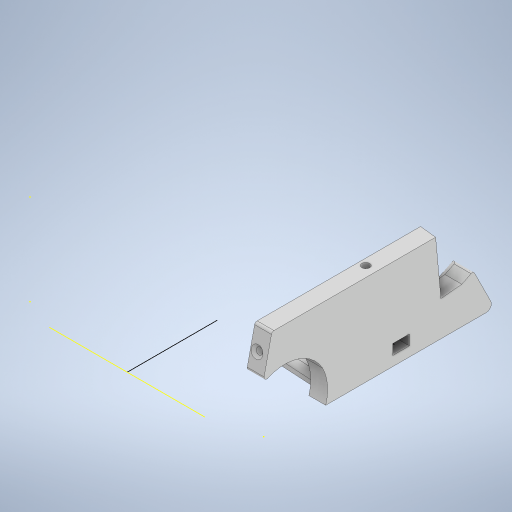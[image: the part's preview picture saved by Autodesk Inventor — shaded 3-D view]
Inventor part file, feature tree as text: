
AUTODESK INVENTOR PART (.ipt)
format: ipt  version: 2023 (Build 270158000, 158)  size: 2,900,992 bytes
history: native  units: mm
features: projected_geometry x144, extrude x133, sketch x99, fillet x14, reference x6, other x5, plane x3, mirror x3, chamfer x2
ambient origin geometry x8: Origin, YZ Plane, XZ Plane, XY Plane, X Axis, Y Axis, Z Axis, Center Point
bodies: Solid1 (feature_tree)
feature tree (409):
  sketch  "Sketch1"  dims[d0=100.0mm d1=100.0mm]
  extrude  "Extrusion1"  Depth=100.0mm
  extrude  "Extrusion2"  Depth=20.0mm
  extrude  "Extrusion3"  Depth=20.0mm
  sketch  "Sketch3"  dims[d4=31.0mm d5=20.0mm]
  extrude  "Extrusion4"  Depth=19.0mm
  extrude  "Extrusion5"  Depth=10.0mm
  sketch  "Sketch4"  dims[d6=14.0mm d7=19.0mm]
  plane  "Work Plane1"
  mirror  "Mirror1"
  extrude  "Extrusion6"  Depth=10.0mm
  sketch  "Sketch8"  dims[d10=10.0mm d11=2.0mm]
  extrude  "Extrusion7"  Depth=15.0mm
  extrude  "Extrusion8"  Depth=2.0mm
  extrude  "Extrusion9"  Depth=5.0mm
  sketch  "Sketch9"  dims[d12=2.0mm d13=15.0mm]
  extrude  "Extrusion10"  Depth=10.0mm TaperAngle=0.0deg
  extrude  "Extrusion11"  TaperAngle=0.0deg  [1 undecoded]
  sketch  "Sketch10"  dims[d14=15.0mm d15=2.0mm]
  extrude  "Extrusion12"  Depth=14.0mm TaperAngle=0.0deg
  extrude  "Extrusion13"  TaperAngle=90.0deg  [1 undecoded]
  extrude  "Extrusion14"  Depth=40.0mm
  sketch  "Sketch12"  dims[d18=10.0mm d19=0.0mm d20=2.0mm d21=0.0mm]
  extrude  "Extrusion15"  Depth=25.0mm
  extrude  "Extrusion16"  Depth=5.0mm
  extrude  "Extrusion17"  Depth=13.0mm
  extrude  "Extrusion18"  Depth=8.0mm
  extrude  "Extrusion19"  Depth=18.0mm TaperAngle=0.0deg
  extrude  "Extrusion20"  Depth=49.0mm
  extrude  "Extrusion21"  Depth=5.0mm
  sketch  "Sketch15"  dims[d28=14.25mm d29=0.0mm d30=90.0deg]
  plane  "Work Plane2"
  mirror  "Mirror2"
  extrude  "Extrusion22"  TaperAngle=0.0deg  [1 undecoded]
  sketch  "Sketch17"  dims[d36=15.0mm d37=25.0mm]
  extrude  "Extrusion23"  Depth=10.0mm
  extrude  "Extrusion24"  Depth=1.6mm
  extrude  "Extrusion25"  TaperAngle=0.0deg  [1 undecoded]
  extrude  "Extrusion26"  Depth=14.0mm TaperAngle=0.0deg
  extrude  "Extrusion27"  Depth=6.0mm
  sketch  "Sketch21"  dims[d44=18.0mm d45=0.0mm d46=18.0mm d47=0.0mm]
  extrude  "Extrusion28"  Depth=2.0mm
  extrude  "Extrusion29"  Depth=6.0mm TaperAngle=0.0deg
  sketch  "Sketch22"  dims[d48=0.0mm d49=0.0mm d50=49.0mm]
  extrude  "Extrusion30"  Depth=15.0mm TaperAngle=0.0deg
  extrude  "Extrusion31"  Depth=3.2mm
  extrude  "Extrusion32"  Depth=4.0mm
  extrude  "Extrusion33"  Depth=1.0mm TaperAngle=0.0deg
  extrude  "Extrusion34"  Depth=3.0mm
  extrude  "Extrusion35"  Depth=15.0mm TaperAngle=0.0deg
  extrude  "Extrusion36"  Depth=3.2mm
  fillet  "Face Fillet1"
  fillet  "Face Fillet2"
  extrude  "Extrusion37"  Depth=3.2mm
  fillet  "Face Fillet3"
  fillet  "Face Fillet5"
  extrude  "Extrusion38"  Depth=5.0mm TaperAngle=0.0deg
  extrude  "Extrusion39"  TaperAngle=0.0deg  [1 undecoded]
  fillet  "Fillet2"  Radius=2.8mm
  extrude  "Extrusion40"  Depth=100.0mm TaperAngle=0.0deg
  sketch  "Sketch32"  dims[d76=6.0mm d77=0.0mm d78=15.0mm d79=0.0mm]
  extrude  "Extrusion41"  Depth=11.0mm
  extrude  "Extrusion42"  Depth=9.0mm TaperAngle=0.0deg
  extrude  "Extrusion43"  Depth=3.2mm
  sketch  "Sketch33"  dims[d80=15.0mm d81=0.0mm d82=3.2mm]
  extrude  "Extrusion44"  Depth=7.0mm TaperAngle=0.0deg
  extrude  "Extrusion45"  Depth=40.656mm TaperAngle=0.0deg
  extrude  "Extrusion46"  Depth=9.0mm TaperAngle=0.0deg
  extrude  "Extrusion47"  Depth=3.0mm
  sketch  "Sketch36"  dims[d91=90.0deg d92=3.0mm]
  extrude  "Extrusion48"  Depth=1.5mm TaperAngle=0.0deg
  extrude  "Extrusion49"  Depth=6.0mm
  sketch  "Sketch37"  dims[d93=3.0mm d94=15.0mm d95=0.0mm]
  extrude  "Extrusion50"  Depth=10.0mm TaperAngle=0.0deg
  extrude  "Extrusion51"  Depth=4.0mm
  extrude  "Extrusion52"  Depth=10.0mm TaperAngle=0.0deg
  extrude  "Extrusion53"  Depth=20.0mm TaperAngle=0.0deg
  sketch  "Sketch40"  dims[d100=4.0mm d101=5.0mm d102=0.0mm]
  extrude  "Extrusion54"  Depth=1.5mm
  extrude  "Extrusion55"  Depth=3.0mm
  extrude  "Extrusion56"  Depth=6.4mm
  extrude  "Extrusion57"  Depth=3.0mm
  fillet  "Fillet3"  Radius=2.0mm
  extrude  "Extrusion58"  TaperAngle=0.0deg  [1 undecoded]
  sketch  "Sketch44"  dims[d114=3.4mm d115=9.0mm d116=0.0mm]
  extrude  "Extrusion59"  TaperAngle=0.0deg  [1 undecoded]
  extrude  "Extrusion60"  Depth=10.0mm TaperAngle=0.0deg
  sketch  "Sketch45"  dims[d117=15.0mm d118=0.0mm d119=3.2mm]
  extrude  "Extrusion61"  Depth=10.0mm TaperAngle=0.0deg
  extrude  "Extrusion62"  Depth=3.0mm
  sketch  "Sketch46"  dims[d120=3.2mm d121=7.0mm d122=0.0mm]
  extrude  "Extrusion63"  Depth=6.5mm TaperAngle=0.0deg
  extrude  "Extrusion64"  Depth=17.0mm TaperAngle=0.0deg
  extrude  "Extrusion65"  Depth=3.0mm
  extrude  "Extrusion66"  Depth=5.0mm TaperAngle=0.0deg
  sketch  "Sketch49"  dims[d138=28.734mm d139=3.0mm]
  extrude  "Extrusion67"  Depth=6.5mm TaperAngle=0.0deg
  extrude  "Extrusion68"  Depth=14.0mm TaperAngle=0.0deg
  extrude  "Extrusion69"  Depth=2.0mm
  extrude  "Extrusion70"  Depth=16.0mm TaperAngle=0.0deg
  extrude  "Extrusion71"  Depth=17.0mm TaperAngle=0.0deg
  extrude  "Extrusion72"  Depth=2.5mm
  extrude  "Extrusion73"  Depth=2.0mm
  extrude  "Extrusion74"  TaperAngle=0.0deg  [1 undecoded]
  extrude  "Extrusion75"  Depth=3.0mm TaperAngle=0.0deg
  extrude  "Extrusion76"  Depth=2.5mm
  sketch  "Sketch53"  dims[d149=6.7mm d152=4.0mm]
  extrude  "Extrusion77"  Depth=1.0mm
  extrude  "Extrusion78"  Depth=3.0mm
  extrude  "Extrusion79"  Depth=15.0mm TaperAngle=0.0deg
  extrude  "Extrusion80"  Depth=10.0mm TaperAngle=0.0deg
  extrude  "Extrusion81"  Depth=10.0mm TaperAngle=0.0deg
  extrude  "Extrusion82"  Depth=4.0mm TaperAngle=0.0deg
  extrude  "Extrusion83"  Depth=10.0mm TaperAngle=0.0deg
  sketch  "Sketch59"  dims[d166=6.4mm d167=3.0mm d169=2.0mm]
  extrude  "Extrusion84"  Depth=7.0mm
  extrude  "Extrusion85"  Depth=3.0mm TaperAngle=0.0deg
  extrude  "Extrusion86"  Depth=4.0mm TaperAngle=0.0deg
  extrude  "Extrusion87"  Depth=1.0mm
  extrude  "Extrusion88"  Depth=10.0mm
  sketch  "Sketch62"  dims[d178=10.0mm d179=0.0mm d180=4.0mm d181=0.0mm]
  extrude  "Extrusion89"  Depth=30.0mm TaperAngle=0.0deg
  extrude  "Extrusion90"  Depth=2.5mm
  fillet  "Fillet4"  Radius=11.0mm
  extrude  "Extrusion91"  TaperAngle=0.0deg  [1 undecoded]
  extrude  "Extrusion92"  Depth=10.0mm
  extrude  "Extrusion93"  Depth=3.0mm
  extrude  "Extrusion94"  Depth=1.0mm TaperAngle=0.0deg
  extrude  "Extrusion95"  Depth=1.5mm TaperAngle=0.0deg
  sketch  "Sketch68"  dims[d205=4.0mm d206=0.0mm d207=5.0mm d208=0.0mm]
  extrude  "Extrusion96"  Depth=10.0mm TaperAngle=0.0deg
  extrude  "Extrusion97"  Depth=10.0mm TaperAngle=0.0deg
  extrude  "Extrusion98"  Depth=10.0mm
  extrude  "Extrusion99"  Depth=10.0mm TaperAngle=0.0deg
  extrude  "Extrusion100"  Depth=10.0mm TaperAngle=0.0deg
  sketch  "Sketch74"  dims[d219=6.5mm d220=0.0mm d221=16.0mm d222=0.0mm]
  extrude  "Extrusion101"  Depth=10.0mm TaperAngle=0.0deg
  extrude  "Extrusion102"  Depth=10.0mm
  extrude  "Extrusion103"  Depth=10.0mm TaperAngle=0.0deg
  extrude  "Extrusion104"  Depth=10.0mm TaperAngle=0.0deg
  extrude  "Extrusion105"  Depth=10.0mm
  fillet  "Fillet6"  Radius=1.5mm
  fillet  "Fillet7"  Radius=3.5mm
  extrude  "Extrusion106"  Depth=10.0mm
  fillet  "Fillet8"  Radius=6.5mm
  extrude  "Extrusion107"  Depth=10.0mm TaperAngle=0.0deg
  sketch  "Sketch80"  dims[d239=1.0mm d240=2.5mm]
  extrude  "Extrusion108"  Depth=10.0mm
  extrude  "Extrusion109"  Depth=10.0mm TaperAngle=0.0deg
  extrude  "Extrusion110"  Depth=10.0mm TaperAngle=0.0deg
  extrude  "Extrusion111"  Depth=10.0mm
  extrude  "Extrusion112"  TaperAngle=90.0deg  [1 undecoded]
  fillet  "Fillet9"  Radius=2.7mm
  extrude  "Extrusion113"  Depth=10.0mm TaperAngle=0.0deg
  extrude  "Extrusion114"  Depth=10.0mm
  extrude  "Extrusion115"  Depth=10.0mm TaperAngle=0.0deg
  plane  "Work Plane3"
  mirror  "Mirror3"
  extrude  "Extrusion116"  Depth=10.0mm TaperAngle=0.0deg
  extrude  "Extrusion117"  Depth=10.0mm TaperAngle=0.0deg
  sketch  "Sketch89"  dims[d269=6.5mm d270=0.0mm d271=3.0mm d272=0.0mm]
  extrude  "Extrusion118"  Depth=10.0mm TaperAngle=0.0deg
  extrude  "Extrusion119"  Depth=10.0mm TaperAngle=0.0deg
  extrude  "Extrusion120"  Depth=10.0mm
  chamfer  "Chamfer1"  Distance=1.0mm
  sketch  "Sketch93"  dims[d282=45.0mm d283=30.0mm d284=0.0mm]
  extrude  "Extrusion121"  Depth=10.0mm TaperAngle=0.0deg
  extrude  "Extrusion122"  Depth=10.0mm
  extrude  "Extrusion123"  Depth=10.0mm
  extrude  "Extrusion124"  Depth=10.0mm TaperAngle=0.0deg
  extrude  "Extrusion125"  Depth=10.0mm TaperAngle=0.0deg
  extrude  "Extrusion126"  Depth=10.0mm TaperAngle=0.0deg
  extrude  "Extrusion127"  Depth=10.0mm TaperAngle=0.0deg
  fillet  "Fillet10"  Radius=6.5mm
  extrude  "Extrusion128"  Depth=10.0mm TaperAngle=0.0deg
  extrude  "Extrusion129"  Depth=10.0mm
  extrude  "Extrusion130"  Depth=10.0mm
  fillet  "Fillet11"  Radius=10.0mm
  fillet  "Fillet12"  Radius=15.0mm
  chamfer  "Chamfer2"  Distance=12.0mm
  extrude  "Wyciągnięcie proste131"  Depth=10.0mm
  extrude  "Wyciągnięcie proste132"  Depth=10.0mm
  extrude  "Wyciągnięcie proste133"  Depth=10.0mm
  sketch  "Sketch2"  dims[d2=5.0mm d3=20.0mm]
  projected_geometry  "Projected Loop1"
  sketch  "Sketch6"  dims[d8=10.0mm d9=14.0mm]
  projected_geometry  "Projected Loop5"
  projected_geometry  "Projected Loop6"
  projected_geometry  "Projected Loop7"
  projected_geometry  "Projected Loop8"
  projected_geometry  "Projected Loop9"
  projected_geometry  "Projected Loop10"
  sketch  "Sketch11"  dims[d16=1.0mm d17=5.0mm]
  projected_geometry  "Projected Loop11"
  projected_geometry  "Projected Loop12"
  sketch  "Sketch13"  dims[d22=31.0mm d23=0.0mm d24=0.0mm]
  projected_geometry  "Projected Loop13"
  projected_geometry  "Projected Loop14"
  sketch  "Sketch14"  dims[d25=30.4mm d26=14.0mm d27=0.0mm]
  projected_geometry  "Projected Loop15"
  projected_geometry  "Projected Loop16"
  sketch  "Sketch16"  dims[d33=25.0mm d34=0.0mm d35=40.0mm]
  projected_geometry  "Projected Loop17"
  projected_geometry  "Projected Loop18"
  projected_geometry  "Projected Loop19"
  sketch  "Sketch18"  dims[d38=20.0mm d39=5.0mm]
  projected_geometry  "Projected Loop20"
  projected_geometry  "Projected Loop21"
  projected_geometry  "Projected Loop22"
  projected_geometry  "Projected Loop23"
  projected_geometry  "Projected Loop24"
  projected_geometry  "Projected Loop25"
  projected_geometry  "Projected Loop26"
  sketch  "Sketch19"  dims[d40=7.0mm d41=13.0mm]
  projected_geometry  "Projected Loop27"
  sketch  "Sketch20"  dims[d42=7.0mm d43=8.0mm]
  projected_geometry  "Projected Loop28"
  projected_geometry  "Projected Loop29"
  projected_geometry  "Projected Loop30"
  sketch  "Sketch23"  dims[d51=25.0mm d52=5.0mm]
  sketch  "Sketch24"  dims[d53=20.0mm d54=0.0mm d55=0.0mm]
  projected_geometry  "Projected Loop31"
  projected_geometry  "Projected Loop32"
  sketch  "Sketch25"  dims[d56=10.0mm d57=0.0mm d58=1.6mm]
  projected_geometry  "Projected Loop33"
  sketch  "Sketch26"  dims[d59=1.6mm d60=1.6mm]
  projected_geometry  "Projected Loop34"
  sketch  "Sketch27"  dims[d61=5.0mm d62=0.0mm d63=0.0mm d64=0.0mm]
  projected_geometry  "Projected Loop35"
  sketch  "Sketch28"  dims[d65=2.5mm d66=14.0mm d67=0.0mm]
  projected_geometry  "Projected Loop36"
  sketch  "Sketch29"  dims[d68=2.0mm d69=6.0mm]
  sketch  "Sketch30"  dims[d70=5.0mm d71=2.0mm]
  projected_geometry  "Projected Loop37"
  projected_geometry  "Projected Loop38"
  projected_geometry  "Projected Loop39"
  sketch  "Sketch31"  dims[d72=14.0mm d73=0.0mm d74=6.0mm d75=0.0mm]
  projected_geometry  "Projected Loop40"
  projected_geometry  "Projected Loop41"
  projected_geometry  "Projected Loop42"
  projected_geometry  "Projected Loop43"
  projected_geometry  "Projected Loop44"
  projected_geometry  "Projected Loop45"
  projected_geometry  "Projected Loop46"
  sketch  "Sketch34"  dims[d83=3.2mm d84=4.0mm]
  projected_geometry  "Projected Loop47"
  projected_geometry  "Projected Loop48"
  sketch  "Sketch35"  dims[d85=15.0mm d86=0.0mm d87=1.0mm d88=0.0mm]
  projected_geometry  "Projected Loop49"
  projected_geometry  "Projected Loop50"
  projected_geometry  "Projected Loop51"
  projected_geometry  "Projected Loop52"
  projected_geometry  "Projected Loop53"
  sketch  "Sketch38"  dims[d96=3.2mm d97=3.2mm]
  projected_geometry  "Projected Loop54"
  projected_geometry  "Projected Loop55"
  sketch  "Sketch39"  dims[d98=3.2mm d99=3.2mm]
  projected_geometry  "Projected Loop56"
  sketch  "Sketch41"  dims[d103=5.0mm d104=0.0mm d105=0.0mm d106=0.0mm d107=2.8mm]
  projected_geometry  "Projected Loop57"
  sketch  "Sketch42"  dims[d108=2.8mm d109=100.0mm d110=0.0mm]
  projected_geometry  "Projected Loop58"
  sketch  "Sketch43"  dims[d111=20.0mm d112=0.0mm d113=11.0mm]
  projected_geometry  "Projected Loop59"
  projected_geometry  "Projected Loop60"
  projected_geometry  "Projected Loop61"
  projected_geometry  "Projected Loop62"
  projected_geometry  "Projected Loop63"
  projected_geometry  "Projected Loop64"
  projected_geometry  "Projected Loop65"
  projected_geometry  "Projected Loop66"
  projected_geometry  "Projected Loop67"
  projected_geometry  "Projected Loop68"
  projected_geometry  "Projected Loop69"
  projected_geometry  "Projected Loop70"
  projected_geometry  "Projected Loop71"
  projected_geometry  "Projected Loop72"
  projected_geometry  "Projected Loop73"
  projected_geometry  "Projected Loop74"
  projected_geometry  "Projected Loop75"
  projected_geometry  "Projected Loop76"
  projected_geometry  "Projected Loop77"
  projected_geometry  "Projected Loop78"
  sketch  "Sketch47"  dims[d123=4.0mm d124=0.0mm d125=40.656mm d126=0.0mm]
  projected_geometry  "Projected Loop79"
  sketch  "Sketch48"  dims[d127=3.0mm d128=0.0mm d129=9.0mm d130=0.0mm]
  projected_geometry  "Projected Loop80"
  projected_geometry  "Projected Loop81"
  sketch  "Sketch50"  dims[d140=1.5mm d141=0.0mm d142=1.5mm d143=0.0mm]
  projected_geometry  "Projected Loop82"
  projected_geometry  "Projected Loop83"
  sketch  "Sketch51"  dims[d144=6.0mm d145=6.0mm]
  projected_geometry  "Projected Loop84"
  sketch  "Sketch52"  dims[d146=2.0mm d147=10.0mm d148=0.0mm]
  projected_geometry  "Projected Loop85"
  projected_geometry  "Projected Loop86"
  projected_geometry  "Projected Loop87"
  sketch  "Sketch54"  dims[d153=10.0mm d154=0.0mm d155=16.0mm d156=0.0mm]
  projected_geometry  "Projected Loop88"
  projected_geometry  "Projected Loop89"
  sketch  "Sketch55"  dims[d157=1e-05mm d158=20.0mm d159=0.0mm]
  projected_geometry  "Projected Loop90"
  projected_geometry  "Projected Loop91"
  sketch  "Sketch56"  dims[d160=6.4mm d161=1.5mm]
  projected_geometry  "Projected Loop92"
  projected_geometry  "Projected Loop93"
  projected_geometry  "Projected Loop94"
  sketch  "Sketch57"  dims[d162=16.5mm d163=3.0mm]
  projected_geometry  "Projected Loop95"
  projected_geometry  "Projected Loop96"
  projected_geometry  "Projected Loop97"
  sketch  "Sketch58"  dims[d164=3.0mm d165=6.4mm]
  projected_geometry  "Projected Loop98"
  projected_geometry  "Projected Loop99"
  projected_geometry  "Projected Loop100"
  projected_geometry  "Projected Loop101"
  sketch  "Sketch60"  dims[d170=5.928mm d171=0.0mm d172=0.0mm d173=0.0mm]
  projected_geometry  "Projected Loop102"
  projected_geometry  "Projected Loop103"
  sketch  "Sketch61"  dims[d174=3.0mm d175=0.0mm d176=0.0mm d177=0.0mm]
  projected_geometry  "Projected Loop104"
  projected_geometry  "Projected Loop105"
  projected_geometry  "Projected Loop106"
  projected_geometry  "Projected Loop107"
  projected_geometry  "Projected Loop108"
  projected_geometry  "Projected Loop109"
  projected_geometry  "Projected Loop110"
  projected_geometry  "Projected Loop111"
  sketch  "Sketch63"  dims[d182=2.5mm d183=10.0mm d184=0.0mm]
  projected_geometry  "Projected Loop112"
  sketch  "Sketch64"  dims[d185=2.0mm d186=3.0mm]
  projected_geometry  "Projected Loop113"
  sketch  "Sketch65"  dims[d195=0.0mm d196=0.0mm d197=6.5mm d198=0.0mm]
  projected_geometry  "Projected Loop114"
  reference  "Reference1"
  sketch  "Sketch66"  dims[d199=2.5mm d200=17.0mm d201=0.0mm]
  reference  "Reference2"
  reference  "Reference3"
  sketch  "Sketch67"  dims[d202=14.0mm d203=0.0mm d204=3.0mm]
  projected_geometry  "Projected Loop115"
  projected_geometry  "Projected Loop116"
  sketch  "Sketch69"  dims[d209=2.5mm d210=6.5mm d211=0.0mm]
  projected_geometry  "Projected Loop117"
  sketch  "Sketch72"  dims[d212=0.0mm d213=0.0mm d214=14.0mm d215=0.0mm]
  projected_geometry  "Projected Loop118"
  sketch  "Sketch73"  dims[d216=6.5mm d217=0.0mm d218=2.0mm]
  projected_geometry  "Projected Loop119"
  projected_geometry  "Projected Loop120"
  sketch  "Sketch75"  dims[d223=17.0mm d224=0.0mm d225=17.0mm d226=0.0mm]
  reference  "Reference4"
  projected_geometry  "Projected Loop121"
  sketch  "Sketch76"  dims[d227=17.0mm d228=0.0mm d229=2.5mm]
  projected_geometry  "Projected Loop122"
  sketch  "Sketch77"  dims[d230=2.5mm d231=2.0mm]
  projected_geometry  "Projected Loop123"
  sketch  "Sketch78"  dims[d232=13.0mm d233=0.0mm d234=0.0mm]
  projected_geometry  "Projected Loop124"
  sketch  "Sketch79"  dims[d235=6.5mm d236=0.0mm d237=3.0mm d238=0.0mm]
  projected_geometry  "Projected Loop125"
  projected_geometry  "Projected Loop126"
  projected_geometry  "Projected Loop127"
  sketch  "Sketch81"  dims[d241=14.0mm d242=0.0mm d243=1.0mm]
  sketch  "Sketch82"  dims[d244=2.0mm d245=3.0mm]
  projected_geometry  "Projected Loop128"
  sketch  "Sketch83"  dims[d246=3.2mm d247=15.0mm d248=0.0mm]
  projected_geometry  "Projected Loop129"
  projected_geometry  "Projected Loop130"
  sketch  "Sketch84"  dims[d249=10.0mm d250=0.0mm d251=10.0mm d252=0.0mm]
  projected_geometry  "Projected Loop131"
  reference  "Reference5"
  projected_geometry  "Projected Loop132"
  sketch  "Sketch85"  dims[d253=3.0mm d254=0.0mm d255=10.0mm d256=0.0mm]
  sketch  "Sketch86"  dims[d257=8.0mm d258=0.0mm d259=4.0mm d260=0.0mm]
  sketch  "Sketch87"  dims[d261=2.5mm d262=10.0mm d263=0.0mm]
  projected_geometry  "Projected Loop133"
  projected_geometry  "Projected Loop134"
  sketch  "Sketch88"  dims[d266=7.0mm d268=7.0mm]
  projected_geometry  "Projected Loop135"
  sketch  "Sketch90"  dims[d273=8.0mm d274=0.0mm d275=4.0mm d276=0.0mm]
  sketch  "Sketch91"  dims[d277=1.0mm d278=1.0mm]
  projected_geometry  "Projected Loop136"
  sketch  "Sketch92"  dims[d279=10.0mm d280=0.0mm d281=1.308997mm]
  projected_geometry  "Projected Loop137"
  projected_geometry  "Projected Loop138"
  sketch  "Sketch94"  dims[d285=2.0mm d286=2.5mm d287=11.0mm d288=0.0mm]
  projected_geometry  "Projected Loop139"
  sketch  "Sketch95"  dims[d289=135.0deg d290=0.0mm d291=0.0mm]
  projected_geometry  "Projected Loop140"
  sketch  "Sketch96"  dims[d292=3.7mm d293=0.0mm d294=10.0mm]
  projected_geometry  "Projected Loop141"
  sketch  "Sketch97"  dims[d295=6.4mm d296=3.0mm]
  projected_geometry  "Projected Loop142"
  reference  "Reference6"
  sketch  "Sketch98"  dims[d297=0.0mm d298=0.0mm d299=1.0mm d300=0.0mm]
  projected_geometry  "Projected Loop143"
  sketch  "Sketch99"  dims[d301=1.5mm d302=0.0mm d303=5.928mm d304=0.0mm]
  projected_geometry  "Projected Loop144"
  sketch  "Sketch100"  dims[d305=12.0mm d306=0.0mm d307=12.0mm d308=0.0mm d309=12.0mm d310=0.0mm d311=2.0mm d312=41.5mm d313=0.0mm d314=5.0mm d315=0.0mm d316=6.5mm d317=0.0mm d318=2.5mm d319=15.0mm d320=0.0mm d321=15.0mm d322=0.0mm d323=6.4mm d324=1.5mm d325=3.5mm d326=3.5mm d327=6.5mm d328=0.0mm d329=6.5mm d330=0.0mm d331=1.047198mm d332=11.908mm d333=0.0mm d334=12.0mm d335=0.0mm d336=8.0mm d337=90.0deg d338=2.7mm d339=10.0mm d340=0.0mm d341=6.4mm d342=10.0mm d343=0.0mm d344=6.5mm d345=0.0mm d346=6.5mm d347=0.0mm d348=6.5mm d349=0.0mm d350=6.5mm d351=0.0mm d353=1.0mm d354=1.0mm d355=6.5mm d356=0.0mm d357=1.0mm d358=2.0mm d359=6.5mm d360=0.0mm d361=4.0mm d362=0.0mm d363=4.0mm d364=0.0mm d365=44.0mm d366=0.0mm d367=6.5mm d368=0.0mm d369=6.5mm d370=0.0mm d371=1.0mm d372=4.0mm d373=10.0mm d374=0.0mm d375=15.0mm d376=0.0mm d377=12.0mm d378=0.0mm d379=41.75mm d380=6.0mm d381=6.0mm d382=6.5mm d383=0.0mm d384=4.0mm d385=0.0mm d386=0.0mm d387=0.0mm d388=1.5mm d389=1.5mm d390=10.0mm d391=0.0mm d392=3.0mm d393=5.0mm d394=0.0mm d395=1.0mm d396=2.0mm d397=45.0deg d398=9.0mm d399=8.0mm d400=0.0mm d401=6.5mm d402=0.0mm d403=6.5mm d404=0.0mm d405=6.5mm d406=0.0mm d407=10.0mm d408=0.0mm d409=6.5mm d410=0.0mm d411=6.5mm d412=0.0mm d413=0.4mm d414=6.5mm d415=0.0mm d416=2.0mm d417=14.0mm d418=0.0mm d419=6.5mm d420=0.0mm d421=0.4mm d422=10.0mm d423=1.0mm d424=2.0mm d425=45.0deg d426=10.0mm d427=0.0mm d428=10.0mm d429=0.0mm d430=10.0mm d431=0.0mm d150=0.0mm d151=0.0mm d352=0.0mm]
  projected_geometry  "Projected Loop145"
  sketch  "Szkic101"
  projected_geometry  "Pętla rzutowana146"
  sketch  "Szkic102"
  projected_geometry  "Pętla rzutowana147"
  sketch  "Szkic103"
  parser-record x1  (decoder bookkeeping rows leaked as tree rows — omitted from the tree; the rows remain in map.json)
  other  "zlozenie.iam"
  other  "sciana_lewa_v4:1"
  other  "<userpath>\Desktop\MojeRoboty\Stefan\mechanics\zlozenie.iam"
  other  "sciana_lewa_v5:1"
note: 10 required parameter values undecoded (feature->parameter linkage not recoverable at this tier; creation-order binding heuristic only, values carry confidence <= 0.55)
note: 1 file-system path scrubbed to <path> (originals preserved in map.json)
